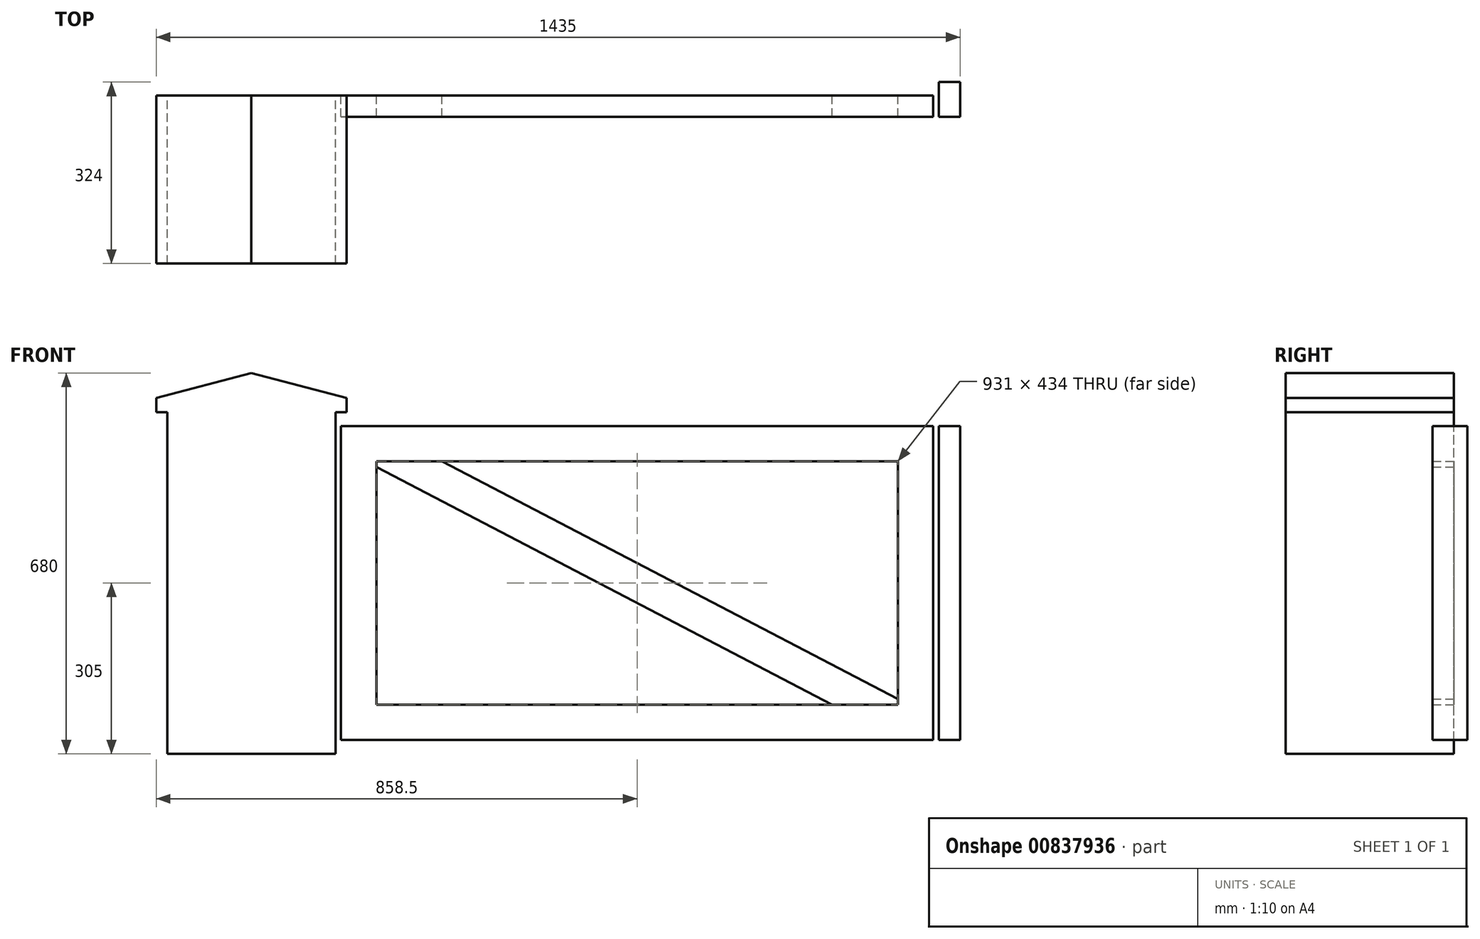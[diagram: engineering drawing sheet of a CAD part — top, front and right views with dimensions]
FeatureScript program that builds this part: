
annotation { "Feature Type Name" : "Feature", "Feature Type Description" : "" }
export const myFeature = defineFeature(function(context is Context, id is Id, definition is map)
    precondition{}
    {
        {
            var Q0;
            Q0=qCreatedBy(makeId("Front.planeOp"),FACE);
            var sketch = newSketch(context, id + "F0", { "sketchPlane" : qUnion([Q0])});
            skLineSegment(sketch, "E0.bottom", {"start": v(0, 0) * mm, "end": v(931, 0) * mm});
            skLineSegment(sketch, "E0.top", {"start": v(0, 63) * mm, "end": v(931, 63) * mm});
            skLineSegment(sketch, "E0.left", {"start": v(0, 0) * mm, "end": v(0, 63) * mm});
            skLineSegment(sketch, "E0.right", {"start": v(931, 0) * mm, "end": v(931, 63) * mm});
            skLineSegment(sketch, "E1.bottom", {"start": v(0, 0) * mm, "end": v(-63, 0) * mm});
            skLineSegment(sketch, "E1.top", {"start": v(0, 560) * mm, "end": v(-63, 560) * mm});
            skLineSegment(sketch, "E1.left", {"start": v(0, 0) * mm, "end": v(0, 560) * mm});
            skLineSegment(sketch, "E1.right", {"start": v(-63, 0) * mm, "end": v(-63, 560) * mm});
            skLineSegment(sketch, "E2.bottom", {"start": v(931, 0) * mm, "end": v(994, 0) * mm});
            skLineSegment(sketch, "E2.top", {"start": v(931, 560) * mm, "end": v(994, 560) * mm});
            skLineSegment(sketch, "E2.left", {"start": v(931, 0) * mm, "end": v(931, 560) * mm});
            skLineSegment(sketch, "E2.right", {"start": v(994, 0) * mm, "end": v(994, 560) * mm});
            skLineSegment(sketch, "E3.bottom", {"start": v(0, 560) * mm, "end": v(931, 560) * mm});
            skLineSegment(sketch, "E3.top", {"start": v(0, 497) * mm, "end": v(931, 497) * mm});
            skLineSegment(sketch, "E3.left", {"start": v(0, 560) * mm, "end": v(0, 497) * mm});
            skLineSegment(sketch, "E3.right", {"start": v(931, 560) * mm, "end": v(931, 497) * mm});
            skLineSegment(sketch, "E4.bottom", {"start": v(1004, 560) * mm, "end": v(1042, 560) * mm});
            skLineSegment(sketch, "E4.top", {"start": v(1004, 0) * mm, "end": v(1042, 0) * mm});
            skLineSegment(sketch, "E4.left", {"start": v(1004, 560) * mm, "end": v(1004, 0) * mm});
            skLineSegment(sketch, "E4.right", {"start": v(1042, 560) * mm, "end": v(1042, 0) * mm});
            skSolve(sketch);
        }
        {
            var Q0;
            Q0 = qSketchRegion(id + "F0", true);
            extrude(context, id + "F1", {"entities" : qUnion([Q0]), "depth" : 38 * mm, "offsetDistance" : 25 * mm});
        }
        {
            var Q0;
            Q0=makeQuery(id+"F1.opExtrude","CAP_FACE",FACE,{"disambiguationData":[OSD([sQuery(id+"F0.wireOp",EDGE,"E4.bottom"),sQuery(id+"F0.wireOp",EDGE,"E4.top"),sQuery(id+"F0.wireOp",EDGE,"E4.left"),sQuery(id+"F0.wireOp",EDGE,"E4.right")])],"isStart":true});
            extrude(context, id + "F2", {"entities" : qUnion([Q0]), "operationType" : NewBodyOperationType.ADD, "depth" : 24 * mm, "offsetDistance" : 25 * mm});
        }
        {
            var Q0;
            Q0=qCreatedBy(makeId("Front.planeOp"),FACE);
            var sketch = newSketch(context, id + "F3", { "sketchPlane" : qUnion([Q0])});
            skLineSegment(sketch, "E5", {"start": v(117.16, 497) * mm, "end": v(931, 73) * mm});
            skLineSegment(sketch, "E6", {"start": v(0, 487) * mm, "end": v(813.84, 63) * mm});
            skLineSegment(sketch, "E7", {"start": v(0, 487) * mm, "end": v(0, 497) * mm});
            skLineSegment(sketch, "E8", {"start": v(0, 497) * mm, "end": v(117.16, 497) * mm});
            skLineSegment(sketch, "E9", {"start": v(813.84, 63) * mm, "end": v(931, 63) * mm});
            skLineSegment(sketch, "E10", {"start": v(931, 63) * mm, "end": v(931, 73) * mm});
            skSolve(sketch);
        }
        {
            var Q0;
            Q0 = qSketchRegion(id + "F3", true);
            extrude(context, id + "F4", {"entities" : qUnion([Q0]), "depth" : 38 * mm, "offsetDistance" : 25 * mm});
        }
        {
            var Q0;
            Q0=qCreatedBy(makeId("Front.planeOp"),FACE);
            var sketch = newSketch(context, id + "F5", { "sketchPlane" : qUnion([Q0])});
            skLineSegment(sketch, "E11.bottom", {"start": v(-73, -25) * mm, "end": v(-373, -25) * mm});
            skLineSegment(sketch, "E11.top", {"start": v(-73, 585) * mm, "end": v(-373, 585) * mm});
            skLineSegment(sketch, "E11.left", {"start": v(-73, -25) * mm, "end": v(-73, 585) * mm});
            skLineSegment(sketch, "E11.right", {"start": v(-373, -25) * mm, "end": v(-373, 585) * mm});
            skLineSegment(sketch, "E12", {"start": v(-73, 280) * mm, "end": v(-373, 280) * mm, "construction": true});
            skLineSegment(sketch, "E13", {"start": v(-393, 585) * mm, "end": v(-53, 585) * mm});
            skLineSegment(sketch, "E14", {"start": v(-53, 585) * mm, "end": v(-53, 610) * mm});
            skLineSegment(sketch, "E15", {"start": v(-53, 610) * mm, "end": v(-223, 655) * mm});
            skPoint(sketch, "E15.endSnap0", {"position": v(-223, 585) * mm});
            skLineSegment(sketch, "E16", {"start": v(-223, 655) * mm, "end": v(-393, 610) * mm});
            skLineSegment(sketch, "E17", {"start": v(-393, 610) * mm, "end": v(-393, 585) * mm});
            skSolve(sketch);
        }
        {
            var Q0;
            Q0 = qSketchRegion(id + "F5", true);
            extrude(context, id + "F6", {"entities" : qUnion([Q0]), "depth" : 300 * mm, "offsetDistance" : 25 * mm});
        }
    });
